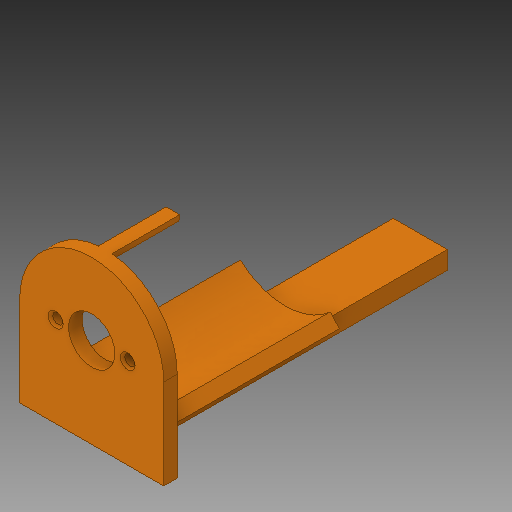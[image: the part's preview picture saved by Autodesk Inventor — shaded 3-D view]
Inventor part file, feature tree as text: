
AUTODESK INVENTOR PART (.ipt)
format: ipt  version: 2018 (Build 220112000, 112)  size: 166,912 bytes
history: native  units: mm
features: sketch x5, extrude x5, other x2, hole x1, chamfer x1, reference x1
ambient origin geometry x8: Origin, YZ Plane, XZ Plane, XY Plane, X Axis, Y Axis, Z Axis, Center Point
bodies: Solid1 (feature_tree)
feature tree (15):
  sketch  "Sketch1"  dims[d0=10.3mm d1=32.0mm]
  extrude  "Extrusion1"  Depth=32.0mm
  hole  "Hole1"  [1 undecoded]
  extrude  "Extrusion2"  Depth=3.0mm TaperAngle=0.0deg
  extrude  "Extrusion3"  Depth=3.0mm
  chamfer  "Chamfer1"  Distance=15.0mm
  extrude  "Extrusion4"  Depth=3.0mm
  extrude  "Extrusion5"  Depth=12.0mm
  sketch  "Sketch2"  dims[d3=20.0mm d4=8.0mm]
  sketch  "Sketch3"  dims[d5=8.0mm d6=3.0mm d7=0.0mm]
  reference  "Reference1"
  sketch  "Sketch4"  dims[d8=2.3mm d9=6.0mm d10=4.0mm d11=2.0mm d12=90.0deg d13=8.0mm d14=20.594885mm d15=3.0mm]
  sketch  "Sketch6"  dims[d16=1.25mm d17=15.0mm d18=0.0mm d19=3.0mm d20=12.0mm d21=24.0mm d22=12.0mm d23=40.0mm d24=0.0mm d25=0.5mm d26=2.0mm d27=45.0deg d28=1.5mm d29=4.0mm d30=30.0mm d31=0.0mm d36=2.3mm d37=9.3mm d38=6.0mm d39=0.0mm]
  other  "Default Motor Testbench Mk2.iam"
  other  "JD5B-2655W-R:1"
note: 1 required parameter value undecoded (feature->parameter linkage not recoverable at this tier; creation-order binding heuristic only, values carry confidence <= 0.55)
